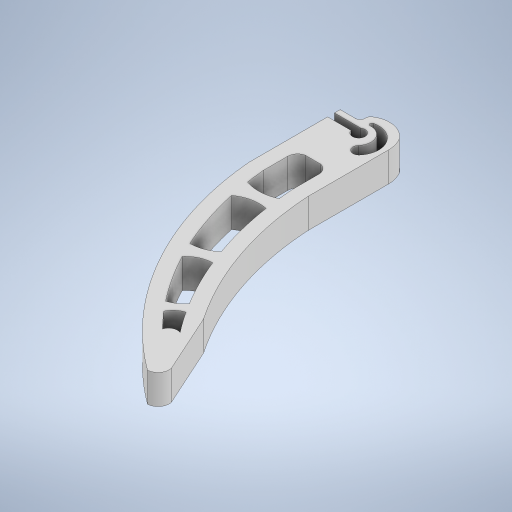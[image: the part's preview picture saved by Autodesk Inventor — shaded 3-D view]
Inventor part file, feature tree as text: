
AUTODESK INVENTOR PART (.ipt)
format: ipt  version: 2024 (Build 280153000, 153)  size: 827,904 bytes
history: native  units: in
note: dims shown in document units (in); Inventor stores cm internally (conversion verified against a paired STEP export)
features: sketch x8, extrude x5, fillet x3, hole x2, projected_geometry x1
ambient origin geometry x8: Origin, YZ Plane, XZ Plane, XY Plane, X Axis, Y Axis, Z Axis, Center Point
bodies: Solid1 (feature_tree)
feature tree (19):
  extrude  "Extrusion1"  Depth=0.175in
  fillet  "Fillet1"  Radius=2.0in
  hole  "Hole1"  [1 undecoded]
  hole  "Hole2"  [1 undecoded]
  extrude  "Extrusion2"  Depth=0.25in
  extrude  "Extrusion4"  Depth=0.75in
  fillet  "Fillet2"  Radius=1.1671in
  fillet  "Fillet3"  Radius=0.75in
  sketch  "Sketch9"  dims[d44=0.2in d45=0.375in d46=0.21in d47=0.75in d48=0.375in d49=0.25in d50=0.5635in d51=1.0in d52=0.0in d53=0.22in d54=0.75in d55=0.375in d56=0.25in d57=0.5635in d58=0.4in d59=0.0in d63=0.2in d65=0.26in d66=0.26in d67=0.7in d68=0.45in d69=0.0in d90=0.12in d91=0.1in d92=1.0in d93=0.0in d94=0.125in d95=0.125in d96=0.403in d97=1.0in d98=0.0in d99=1.0in d100=0.0in]
  extrude  "FOR EXTERIOR"  Depth=0.36in
  extrude  "For Exterior claw"  Depth=0.05in
  sketch  "Sketch1"  dims[d17=0.318in d19=0.175in d22=2.0in]
  sketch  "Sketch2"  dims[d26=0.36in d27=0.35in]
  sketch  "Sketch3"  dims[d28=0.35in d29=0.36in]
  sketch  "Sketch4"  dims[d31=180.0deg d32=0.25in]
  projected_geometry  "Projected Loop1"
  sketch  "Sketch6"  dims[d33=8.1548in d34=1.3328in d35=1.1671in d36=0.75in]
  sketch  "Sketch7"  dims[d37=0.1334in d39=0.36in]
  sketch  "Sketch8"  dims[d40=0.75in d41=0.0in d43=0.05in]
note: 2 required parameter values undecoded (feature->parameter linkage not recoverable at this tier; creation-order binding heuristic only, values carry confidence <= 0.55)
